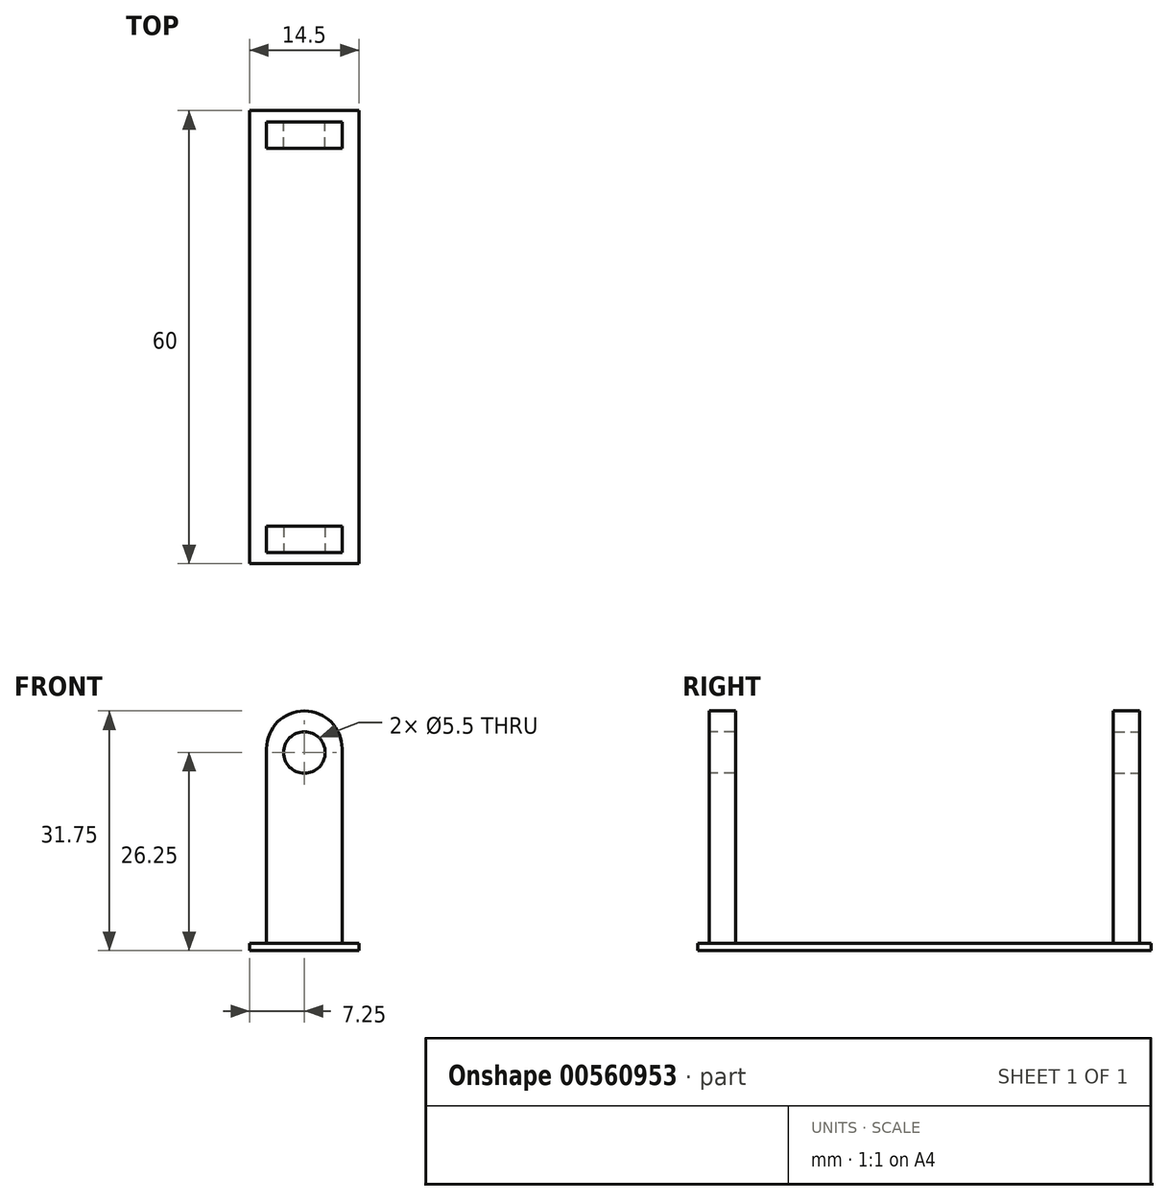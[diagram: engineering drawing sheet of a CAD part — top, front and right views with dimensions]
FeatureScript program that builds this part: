
annotation { "Feature Type Name" : "Feature", "Feature Type Description" : "" }
export const myFeature = defineFeature(function(context is Context, id is Id, definition is map)
    precondition{}
    {
        {
            var Q0;
            Q0=qCreatedBy(makeId("Front.planeOp"),FACE);
            var sketch = newSketch(context, id + "F0", { "sketchPlane" : qUnion([Q0])});
            skLineSegment(sketch, "E0.bottom", {"start": v(0, 0) * mm, "end": v(10, 0) * mm});
            skLineSegment(sketch, "E0.top", {"start": v(5, 30.75) * mm, "end": v(5, 30.75) * mm});
            skLineSegment(sketch, "E0.left", {"start": v(0, 0) * mm, "end": v(0, 25.75) * mm});
            skLineSegment(sketch, "E0.right", {"start": v(10, 0) * mm, "end": v(10, 25.75) * mm});
            skCircle(sketch, "E1", {"center": v(5, 25.25) * mm, "radius": 2.75 * mm});
            skLineSegment(sketch, "E2", {"start": v(5, 25.25) * mm, "end": v(10, 25.25) * mm, "construction": true});
            skLineSegment(sketch, "E3", {"start": v(5, 25.25) * mm, "end": v(0, 25.25) * mm, "construction": true});
            skPoint(sketch, "E4.visualSharp", {"position": v(0, 30.75) * mm});
            skArc(sketch, "E4.filletArc", {"start": v(5, 30.75) * mm, "mid": v(1.46, 29.29) * mm, "end": v(0, 25.75) * mm});
            skPoint(sketch, "E5.visualSharp", {"position": v(10, 30.75) * mm});
            skArc(sketch, "E5.filletArc", {"start": v(10, 25.75) * mm, "mid": v(8.54, 29.29) * mm, "end": v(5, 30.75) * mm});
            skSolve(sketch);
        }
        {
            var Q0;
            Q0=makeQuery(id+"F0.imprint","IMPRINT",FACE,{"disambiguationData":[TD([[makeQuery(id+"F0.imprint","IMPRINT",EDGE,{"derivedFrom":sQuery(id+"F0.wireOp",EDGE,"E0.bottom")}),1.0]])]});
            extrude(context, id + "F1", {"entities" : qUnion([Q0]), "depth" : 3.5 * mm, "offsetDistance" : 25 * mm});
        }
        {
            var Q0;
            Q0=makeQuery(id+"F1.opExtrude","SWEPT_FACE",FACE,{"disambiguationData":[OSD([sQuery(id+"F0.wireOp",EDGE,"E0.bottom")])]});
            var sketch = newSketch(context, id + "F2", { "sketchPlane" : qUnion([Q0])});
            skLineSegment(sketch, "E6.bottom", {"start": v(12.25, 28.5) * mm, "end": v(-2.25, 28.5) * mm});
            skLineSegment(sketch, "E6.top", {"start": v(12.25, -1.5) * mm, "end": v(-2.25, -1.5) * mm});
            skLineSegment(sketch, "E6.left", {"start": v(12.25, 28.5) * mm, "end": v(12.25, -1.5) * mm});
            skLineSegment(sketch, "E6.right", {"start": v(-2.25, 28.5) * mm, "end": v(-2.25, -1.5) * mm});
            skSolve(sketch);
        }
        {
            var Q0;
            Q0=makeQuery(id+"F2.imprint","IMPRINT",FACE,{"disambiguationData":[TD([[makeQuery(id+"F2.imprint","IMPRINT",EDGE,{"derivedFrom":sQuery(id+"F2.wireOp",EDGE,"E6.bottom")}),1.0]])]});
            var Q1;
            {var subQ0=sQuery(id+"F0.wireOp",EDGE,"E0.bottom");Q1=makeQuery(id+"F2.imprint","IMPRINT",FACE,{"disambiguationData":[TD([[makeQuery(id+"F2.imprint","IMPRINT",EDGE,{"derivedFrom":makeQuery(id+"F1.opExtrude","CAP_EDGE",EDGE,{"disambiguationData":[OSD([subQ0])],"isStart":true})}),1.0]])]});}
            extrude(context, id + "F3", {"entities" : qUnion([Q0, Q1]), "operationType" : NewBodyOperationType.ADD, "depth" : 1 * mm, "offsetDistance" : 25 * mm});
        }
        {
            var Q0;
            Q0=makeQuery(id+"F1.opExtrude","SWEPT_BODY",BODY,{"disambiguationData":[OSD([sQuery(id+"F0.wireOp",EDGE,"E0.bottom"),sQuery(id+"F0.wireOp",EDGE,"E0.left"),sQuery(id+"F0.wireOp",EDGE,"E0.right"),sQuery(id+"F0.wireOp",EDGE,"E1"),sQuery(id+"F0.wireOp",EDGE,"E4.filletArc"),sQuery(id+"F0.wireOp",EDGE,"E5.filletArc")])]});
            var Q1;
            Q1=makeQuery(id+"F3.opExtrude","SWEPT_FACE",FACE,{"disambiguationData":[OSD([sQuery(id+"F2.wireOp",EDGE,"E6.bottom")])]});
            mirror(context, id + "F4", {"operationType" : NewBodyOperationType.ADD, "entities" : qUnion([Q0]), "mirrorPlane" : qUnion([Q1])});
        }
    });
